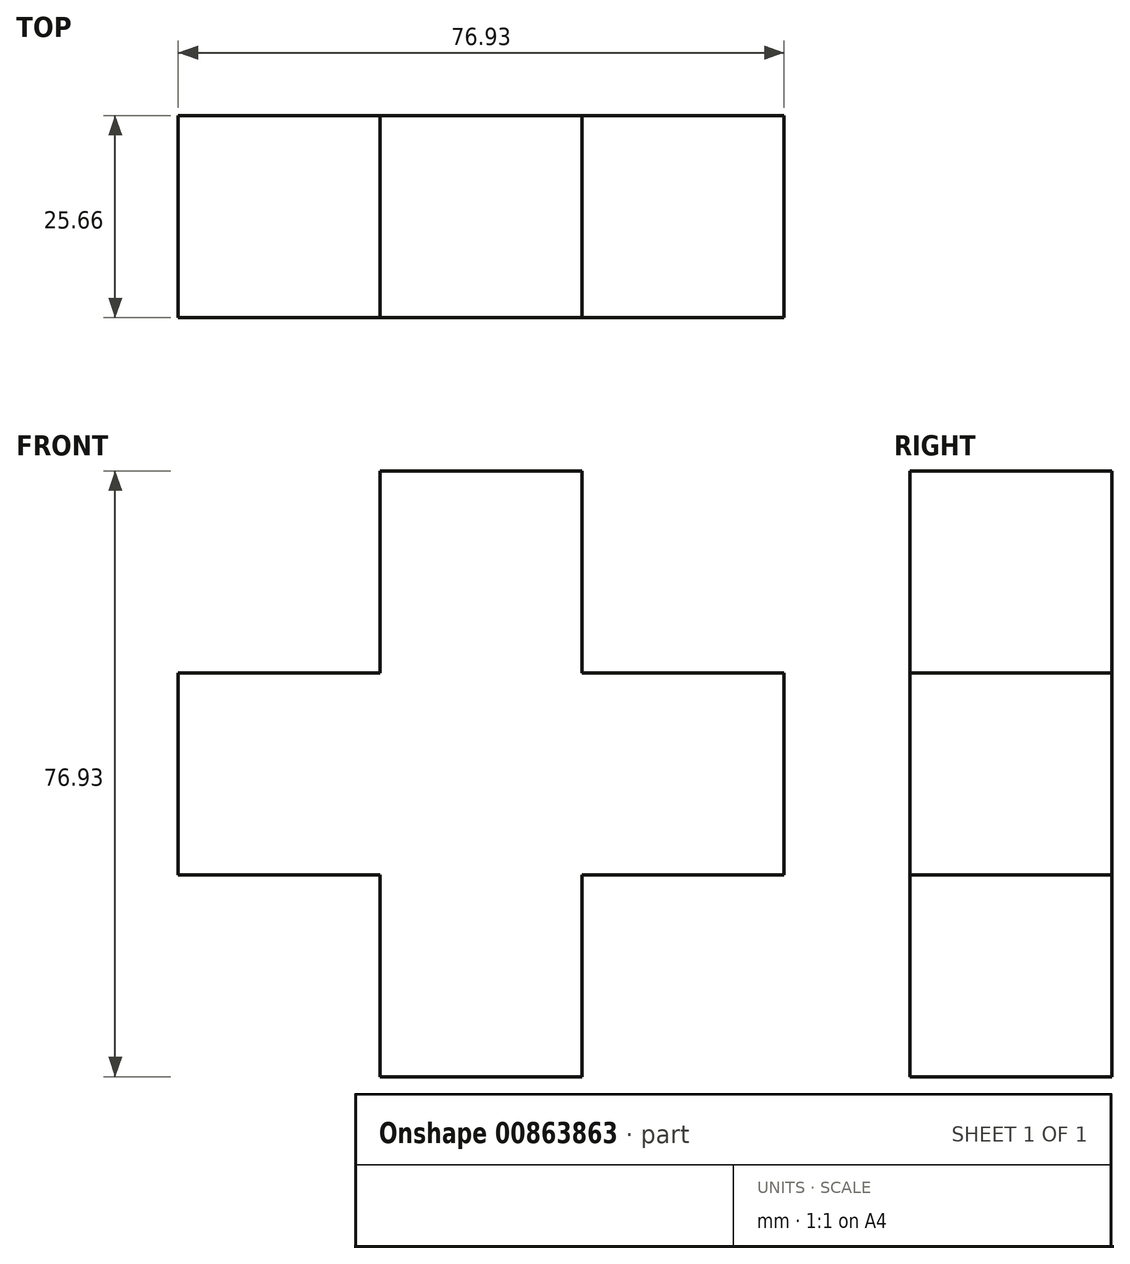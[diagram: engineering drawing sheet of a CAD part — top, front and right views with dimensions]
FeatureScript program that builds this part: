
annotation { "Feature Type Name" : "Feature", "Feature Type Description" : "" }
export const myFeature = defineFeature(function(context is Context, id is Id, definition is map)
    precondition{}
    {
        {
            var Q0;
            Q0=qCreatedBy(makeId("Front.planeOp"),FACE);
            var sketch = newSketch(context, id + "F0", { "sketchPlane" : qUnion([Q0])});
            skLineSegment(sketch, "E0", {"start": v(-35.26, 17.25) * mm, "end": v(-35.26, 42.9) * mm});
            skLineSegment(sketch, "E1", {"start": v(-35.26, 42.9) * mm, "end": v(-9.62, 42.9) * mm});
            skLineSegment(sketch, "E2", {"start": v(-9.62, 42.9) * mm, "end": v(-9.62, 17.25) * mm});
            skLineSegment(sketch, "E3", {"start": v(-9.62, 17.25) * mm, "end": v(16.03, 17.25) * mm});
            skLineSegment(sketch, "E4", {"start": v(16.03, 17.25) * mm, "end": v(16.03, -8.4) * mm});
            skLineSegment(sketch, "E5", {"start": v(-35.26, 17.25) * mm, "end": v(-60.9, 17.25) * mm});
            skLineSegment(sketch, "E6", {"start": v(-60.9, 17.25) * mm, "end": v(-60.9, -8.4) * mm});
            skLineSegment(sketch, "E7", {"start": v(-60.9, -8.4) * mm, "end": v(-35.26, -8.4) * mm});
            skLineSegment(sketch, "E8", {"start": v(-35.26, -8.4) * mm, "end": v(-35.26, -34.04) * mm});
            skLineSegment(sketch, "E9", {"start": v(-35.26, -34.04) * mm, "end": v(-9.62, -34.04) * mm});
            skLineSegment(sketch, "E10", {"start": v(-9.62, -34.04) * mm, "end": v(-9.62, -8.4) * mm});
            skLineSegment(sketch, "E11", {"start": v(-9.62, -8.4) * mm, "end": v(16.03, -8.4) * mm});
            skSolve(sketch);
        }
        {
            var Q0;
            Q0=makeQuery(id+"F0.imprint","IMPRINT",FACE,{"disambiguationData":[TD([[makeQuery(id+"F0.imprint","IMPRINT",EDGE,{"derivedFrom":sQuery(id+"F0.wireOp",EDGE,"E0")}),-1.0]])]});
            extrude(context, id + "F1", {"entities" : qUnion([Q0]), "endBound" : BoundingType.SYMMETRIC, "depth" : 25.65 * mm, "offsetDistance" : 25.4 * mm});
        }
    });
